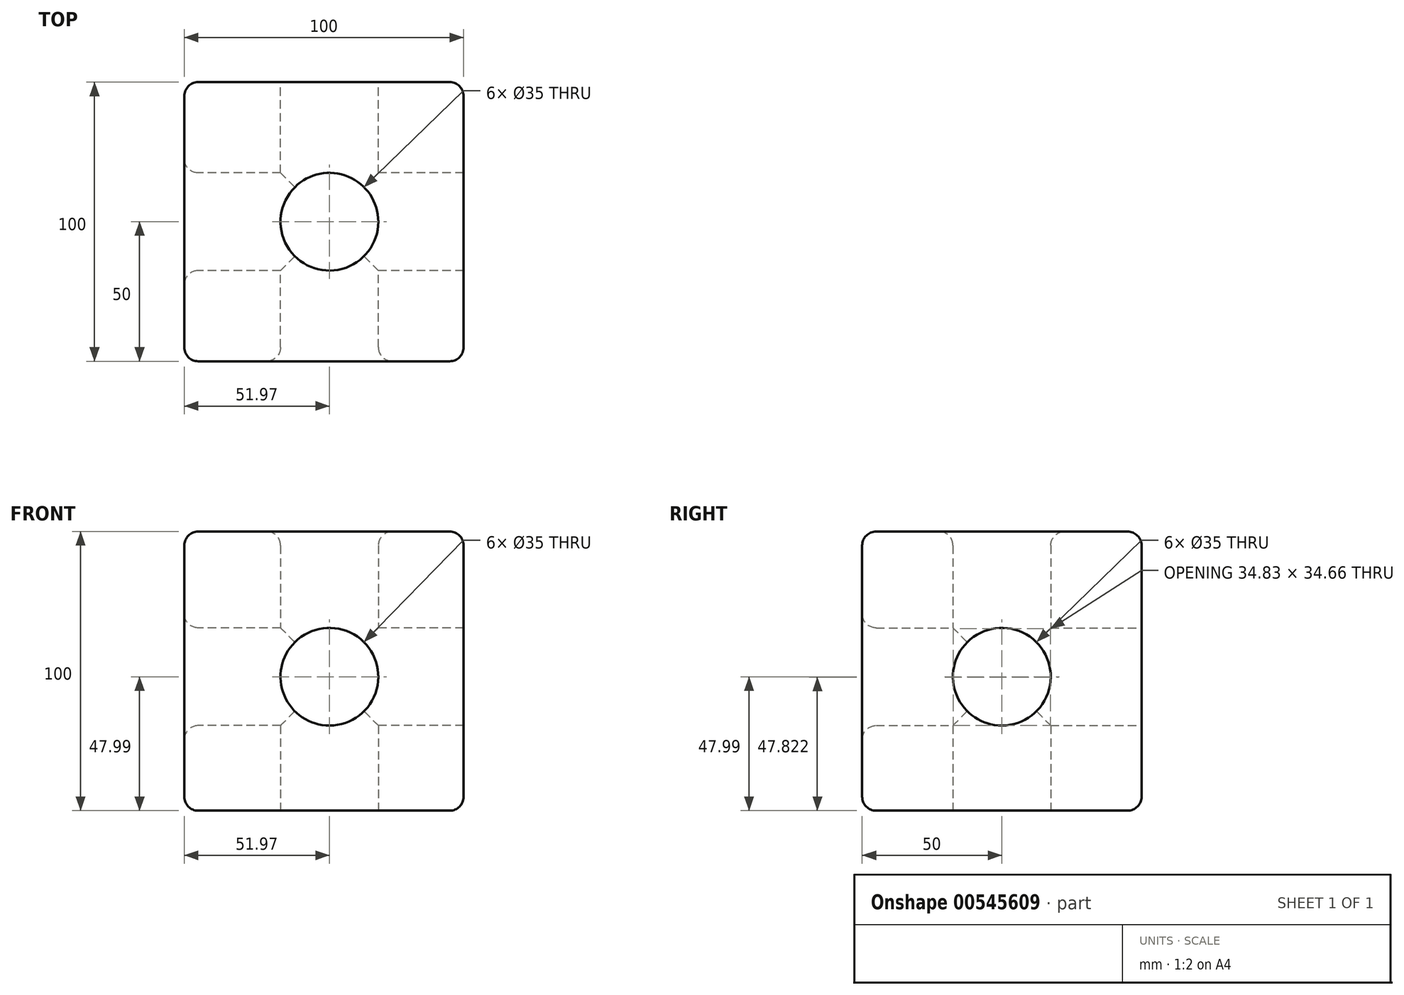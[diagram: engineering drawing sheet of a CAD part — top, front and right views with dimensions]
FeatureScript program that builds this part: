
annotation { "Feature Type Name" : "Feature", "Feature Type Description" : "" }
export const myFeature = defineFeature(function(context is Context, id is Id, definition is map)
    precondition{}
    {
        {
            var Q0;
            Q0=qCreatedBy(makeId("Front.planeOp"),FACE);
            var sketch = newSketch(context, id + "F0", { "sketchPlane" : qUnion([Q0])});
            skLineSegment(sketch, "E0.bottom", {"start": v(-51.97, 52) * mm, "end": v(48.03, 52) * mm});
            skLineSegment(sketch, "E0.top", {"start": v(-51.97, -48) * mm, "end": v(48.03, -48) * mm});
            skLineSegment(sketch, "E0.left", {"start": v(-51.97, 52) * mm, "end": v(-51.97, -48) * mm});
            skLineSegment(sketch, "E0.right", {"start": v(48.03, 52) * mm, "end": v(48.03, -48) * mm});
            skSolve(sketch);
        }
        {
            var Q0;
            Q0=makeQuery(id+"F0.imprint","IMPRINT",FACE,{"disambiguationData":[TD([[makeQuery(id+"F0.imprint","IMPRINT",EDGE,{"derivedFrom":sQuery(id+"F0.wireOp",EDGE,"E0.bottom")}),-1.0]])]});
            extrude(context, id + "F1", {"entities" : qUnion([Q0]), "endBound" : BoundingType.SYMMETRIC, "depth" : 100 * mm, "offsetDistance" : 25 * mm});
        }
        {
            var Q0;
            Q0=makeQuery(id+"F1.opExtrude","SWEPT_FACE",FACE,{"disambiguationData":[OSD([sQuery(id+"F0.wireOp",EDGE,"E0.left")])]});
            var sketch = newSketch(context, id + "F2", { "sketchPlane" : qUnion([Q0])});
            skCircle(sketch, "E1", {"center": v(0, 0) * mm, "radius": 17.5 * mm});
            skSolve(sketch);
        }
        {
            var Q0;
            Q0=makeQuery(id+"F2.imprint","IMPRINT",FACE,{"disambiguationData":[TD([[makeQuery(id+"F2.imprint","IMPRINT",EDGE,{"derivedFrom":sQuery(id+"F2.wireOp",EDGE,"E1")}),1.0]])]});
            extrude(context, id + "F3", {"entities" : qUnion([Q0]), "operationType" : NewBodyOperationType.REMOVE, "endBound" : BoundingType.UP_TO_NEXT, "oppositeDirection" : true, "depth" : 25 * mm, "offsetDistance" : 25 * mm});
        }
        {
            var Q0;
            Q0=makeQuery(id+"F1.opExtrude","CAP_FACE",FACE,{"disambiguationData":[OSD([sQuery(id+"F0.wireOp",EDGE,"E0.bottom"),sQuery(id+"F0.wireOp",EDGE,"E0.top"),sQuery(id+"F0.wireOp",EDGE,"E0.left"),sQuery(id+"F0.wireOp",EDGE,"E0.right")])],"isStart":true});
            var sketch = newSketch(context, id + "F4", { "sketchPlane" : qUnion([Q0])});
            skCircle(sketch, "E2", {"center": v(0, 0) * mm, "radius": 17.5 * mm});
            skSolve(sketch);
        }
        {
            var Q0;
            Q0 = qSketchRegion(id + "F4", true);
            extrude(context, id + "F5", {"entities" : qUnion([Q0]), "operationType" : NewBodyOperationType.REMOVE, "endBound" : BoundingType.THROUGH_ALL, "oppositeDirection" : true, "depth" : 25 * mm, "offsetDistance" : 25 * mm});
        }
        {
            var Q0;
            Q0=makeQuery(id+"F1.opExtrude","SWEPT_FACE",FACE,{"disambiguationData":[OSD([sQuery(id+"F0.wireOp",EDGE,"E0.top")])]});
            var sketch = newSketch(context, id + "F6", { "sketchPlane" : qUnion([Q0])});
            skCircle(sketch, "E3", {"center": v(0, 0) * mm, "radius": 17.5 * mm});
            skSolve(sketch);
        }
        {
            var Q0;
            Q0 = qSketchRegion(id + "F6", true);
            extrude(context, id + "F7", {"entities" : qUnion([Q0]), "operationType" : NewBodyOperationType.REMOVE, "endBound" : BoundingType.THROUGH_ALL, "oppositeDirection" : true, "depth" : 25 * mm, "offsetDistance" : 25 * mm});
        }
        {
            var Q0;
            Q0=makeQuery(id+"F7.boolean.opBoolean","COPY",EDGE,{"derivedFrom":makeQuery(id+"F7.opExtrude","CAP_EDGE",EDGE,{"disambiguationData":[OSD([sQuery(id+"F6.wireOp",EDGE,"E3")])],"isStart":true})});
            var Q1;
            Q1=makeQuery(id+"F5.boolean.opBoolean","COPY",EDGE,{"derivedFrom":makeQuery(id+"F5.opExtrude","CAP_EDGE",EDGE,{"disambiguationData":[OSD([sQuery(id+"F4.wireOp",EDGE,"E2")])],"isStart":true})});
            var Q2;
            Q2=makeQuery(id+"F7.boolean.opBoolean","INTERSECT",EDGE,{"derivedFrom":[makeQuery(id+"F1.opExtrude","SWEPT_FACE",FACE,{"disambiguationData":[OSD([sQuery(id+"F0.wireOp",EDGE,"E0.bottom")])]}),makeQuery(id+"F7.opExtrude","SWEPT_FACE",FACE,{"disambiguationData":[OSD([sQuery(id+"F6.wireOp",EDGE,"E3")])]})]});
            var Q3;
            Q3=makeQuery(id+"F5.boolean.opBoolean","INTERSECT",EDGE,{"derivedFrom":[makeQuery(id+"F1.opExtrude","CAP_FACE",FACE,{"disambiguationData":[OSD([sQuery(id+"F0.wireOp",EDGE,"E0.bottom"),sQuery(id+"F0.wireOp",EDGE,"E0.top"),sQuery(id+"F0.wireOp",EDGE,"E0.left"),sQuery(id+"F0.wireOp",EDGE,"E0.right")])],"isStart":false}),makeQuery(id+"F5.opExtrude","SWEPT_FACE",FACE,{"disambiguationData":[OSD([sQuery(id+"F4.wireOp",EDGE,"E2")])]})]});
            var Q4;
            Q4=makeQuery(id+"F3.boolean.opBoolean","COPY",EDGE,{"derivedFrom":makeQuery(id+"F3.opExtrude","TWEAK_EDGE",EDGE,{"derivedFrom":[makeQuery(id+"F1.opExtrude","SWEPT_FACE",FACE,{"disambiguationData":[OSD([sQuery(id+"F0.wireOp",EDGE,"E0.right")])]}),makeQuery(id+"F2.imprint","IMPRINT",EDGE,{"derivedFrom":sQuery(id+"F2.wireOp",EDGE,"E1")})]})});
            var Q5;
            Q5=makeQuery(id+"F3.boolean.opBoolean","COPY",EDGE,{"derivedFrom":makeQuery(id+"F3.opExtrude","CAP_EDGE",EDGE,{"disambiguationData":[OSD([sQuery(id+"F2.wireOp",EDGE,"E1")])],"isStart":true})});
            var Q6;
            Q6=makeQuery(id+"F1.opExtrude","CAP_EDGE",EDGE,{"disambiguationData":[OSD([sQuery(id+"F0.wireOp",EDGE,"E0.right")])],"isStart":true});
            var Q7;
            Q7=makeQuery(id+"F1.opExtrude","CAP_EDGE",EDGE,{"disambiguationData":[OSD([sQuery(id+"F0.wireOp",EDGE,"E0.bottom")])],"isStart":true});
            var Q8;
            Q8=makeQuery(id+"F1.opExtrude","SWEPT_EDGE",EDGE,{"disambiguationData":[OSD([sQuery(id+"F0.wireOp",EDGE,"E0.bottom"),sQuery(id+"F0.wireOp",EDGE,"E0.left")])]});
            var Q9;
            Q9=makeQuery(id+"F1.opExtrude","CAP_EDGE",EDGE,{"disambiguationData":[OSD([sQuery(id+"F0.wireOp",EDGE,"E0.left")])],"isStart":true});
            var Q10;
            Q10=makeQuery(id+"F1.opExtrude","CAP_EDGE",EDGE,{"disambiguationData":[OSD([sQuery(id+"F0.wireOp",EDGE,"E0.left")])],"isStart":false});
            var Q11;
            Q11=makeQuery(id+"F1.opExtrude","CAP_EDGE",EDGE,{"disambiguationData":[OSD([sQuery(id+"F0.wireOp",EDGE,"E0.top")])],"isStart":true});
            var Q12;
            Q12=makeQuery(id+"F1.opExtrude","SWEPT_EDGE",EDGE,{"disambiguationData":[OSD([sQuery(id+"F0.wireOp",EDGE,"E0.top"),sQuery(id+"F0.wireOp",EDGE,"E0.right")])]});
            var Q13;
            Q13=makeQuery(id+"F1.opExtrude","CAP_EDGE",EDGE,{"disambiguationData":[OSD([sQuery(id+"F0.wireOp",EDGE,"E0.right")])],"isStart":false});
            var Q14;
            Q14=makeQuery(id+"F1.opExtrude","SWEPT_EDGE",EDGE,{"disambiguationData":[OSD([sQuery(id+"F0.wireOp",EDGE,"E0.bottom"),sQuery(id+"F0.wireOp",EDGE,"E0.right")])]});
            var Q15;
            Q15=makeQuery(id+"F1.opExtrude","CAP_EDGE",EDGE,{"disambiguationData":[OSD([sQuery(id+"F0.wireOp",EDGE,"E0.top")])],"isStart":false});
            var Q16;
            Q16=makeQuery(id+"F1.opExtrude","SWEPT_FACE",FACE,{"disambiguationData":[OSD([sQuery(id+"F0.wireOp",EDGE,"E0.left")])]});
            var Q17;
            Q17=makeQuery(id+"F1.opExtrude","CAP_EDGE",EDGE,{"disambiguationData":[OSD([sQuery(id+"F0.wireOp",EDGE,"E0.bottom")])],"isStart":false});
            fillet(context, id + "F8", {"entities" : qUnion([Q0, Q1, Q2, Q3, Q4, Q5, Q6, Q7, Q8, Q9, Q10, Q11, Q12, Q13, Q14, Q15, Q16, Q17]), "radius" : 5 * mm, "tangentPropagation" : true, "allowEdgeOverflow" : false});
        }
    });
